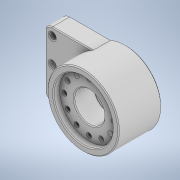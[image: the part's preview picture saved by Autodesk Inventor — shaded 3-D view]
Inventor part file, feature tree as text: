
AUTODESK INVENTOR PART (.ipt)
format: ipt  version: 2020 (Build 240168000, 168)  size: 625,664 bytes
history: native  units: in
note: dims shown in document units (in); Inventor stores cm internally (conversion verified against a paired STEP export)
features: extrude x10, sketch x10, chamfer x3, fillet x1, projected_geometry x1
ambient origin geometry x8: Origin, YZ Plane, XZ Plane, XY Plane, X Axis, Y Axis, Z Axis, Center Point
bodies: Solid1 (feature_tree)
feature tree (25):
  extrude  "Extrusion1"  Depth=1.0in
  fillet  "Fillet1"  Radius=0.2656in
  extrude  "Extrusion2"  Depth=0.3937in
  extrude  "Extrusion3"  Depth=0.3198in
  extrude  "Extrusion4"  TaperAngle=45.0deg  [1 undecoded]
  chamfer  "Chamfer1"  Distance=0.75in
  chamfer  "Chamfer2"  Distance=1.1811in Angle=360.0deg
  extrude  "Extrusion5"  Depth=0.25in
  extrude  "Extrusion6"  Depth=0.25in TaperAngle=0.0deg
  extrude  "Extrusion7"  Depth=0.25in
  extrude  "Extrusion8"  Depth=0.25in TaperAngle=0.0deg
  extrude  "Extrusion9"  Depth=0.25in TaperAngle=45.0deg
  extrude  "Extrusion10"  Depth=0.25in
  chamfer  "Chamfer3"  Distance=2.25in
  sketch  "Sketch1"  dims[d0=1.126in d1=1.0in d2=0.2656in]
  sketch  "Sketch2"  dims[d4=1.1811in d6=1.0in d7=0.3937in d9=1.0in d11=0.3198in]
  sketch  "Sketch3"  dims[d12=0.3198in d13=0.3198in]
  sketch  "Sketch4"  dims[d14=0.813in d15=45.0deg]
  sketch  "Sketch6"  dims[d16=45.0deg d17=0.75in d18=0.0in]
  sketch  "Sketch7"  dims[d19=0.3198in]
  projected_geometry  "Projected Loop1"
  sketch  "Sketch8"  dims[d20=0.7105in]
  sketch  "Sketch9"  dims[d21=0.159in]
  sketch  "Sketch10"  dims[d22=120.0deg d23=1.1811in d25=360.0deg]
  sketch  "Sketch11"  dims[d27=0.0in d28=0.0in d29=1.226in d30=0.064in d31=0.0in d32=1.226in d33=0.064in d34=0.0in d35=0.035in d36=0.125in d37=45.0deg d43=1.225in d45=2.25in d46=1.6375in d47=2.0in d48=1.0in d49=135.0deg d50=0.375in d51=0.125in d52=0.125in d53=45.0deg d54=2.0in d55=2.4in d56=0.25in d57=1.0in d58=0.2031in d59=4.7244in d61=360.0deg d63=0.0in d64=0.0in d65=0.75in d66=0.0in d67=2.4in d68=0.25in d69=0.0in d70=0.4in d71=4.7244in d73=360.0deg d75=0.7in d76=0.0in d77=4.7244in d79=360.0deg d81=0.0118in d82=0.0in d83=4.7244in d85=360.0deg d87=0.0236in d88=0.0in d89=0.035in d90=0.125in d91=45.0deg d78=0.0344in]
note: 1 required parameter value undecoded (feature->parameter linkage not recoverable at this tier; creation-order binding heuristic only, values carry confidence <= 0.55)
